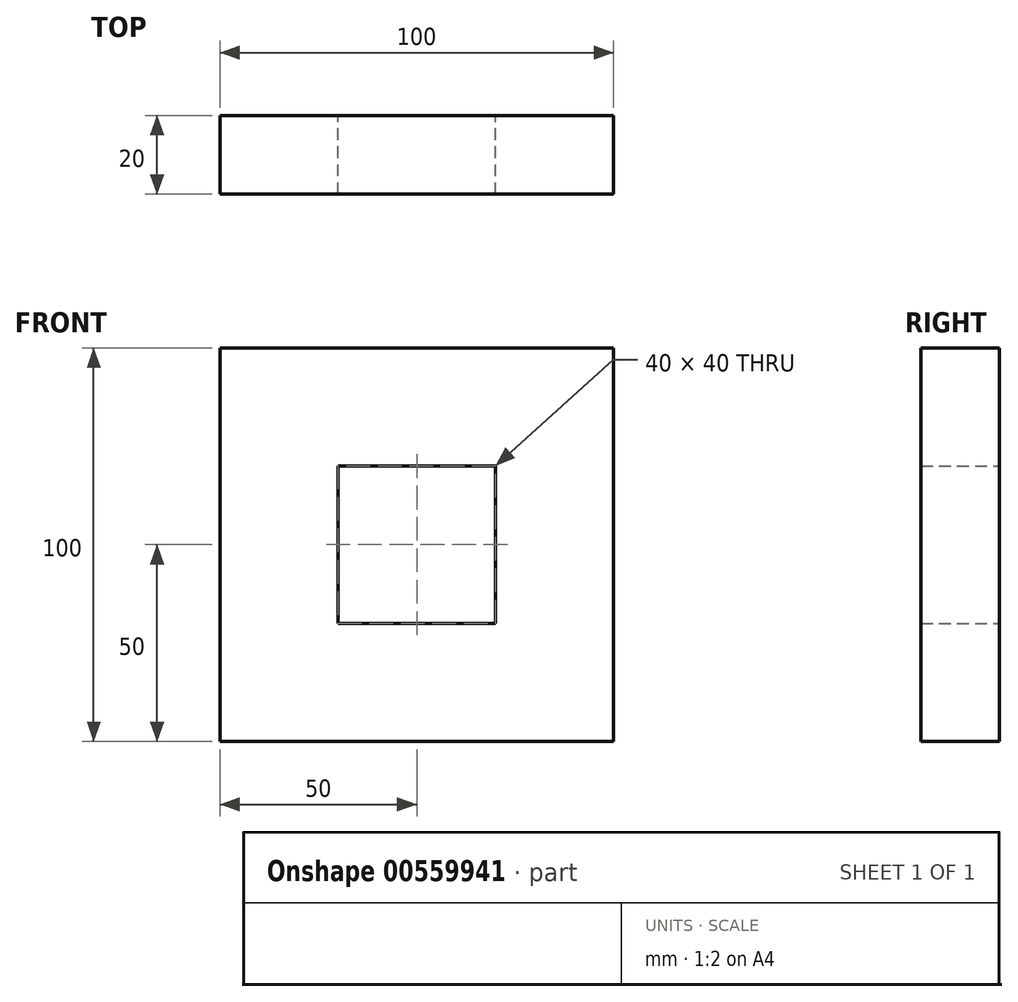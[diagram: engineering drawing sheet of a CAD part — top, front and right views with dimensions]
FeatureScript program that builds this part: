
annotation { "Feature Type Name" : "Feature", "Feature Type Description" : "" }
export const myFeature = defineFeature(function(context is Context, id is Id, definition is map)
    precondition{}
    {
        {
            var Q0;
            Q0=qCreatedBy(makeId("Front.planeOp"),FACE);
            var sketch = newSketch(context, id + "F0", { "sketchPlane" : qUnion([Q0])});
            skLineSegment(sketch, "E0.bottom", {"start": v(50, 50) * mm, "end": v(-50, 50) * mm});
            skLineSegment(sketch, "E0.top", {"start": v(50, -50) * mm, "end": v(-50, -50) * mm});
            skLineSegment(sketch, "E0.left", {"start": v(50, 50) * mm, "end": v(50, -50) * mm});
            skLineSegment(sketch, "E0.right", {"start": v(-50, 50) * mm, "end": v(-50, -50) * mm});
            skPoint(sketch, "E0.middle", {"position": v(0, 0) * mm});
            skLineSegment(sketch, "E1.bottom", {"start": v(20, 20) * mm, "end": v(-20, 20) * mm});
            skLineSegment(sketch, "E1.top", {"start": v(20, -20) * mm, "end": v(-20, -20) * mm});
            skLineSegment(sketch, "E1.left", {"start": v(20, 20) * mm, "end": v(20, -20) * mm});
            skLineSegment(sketch, "E1.right", {"start": v(-20, 20) * mm, "end": v(-20, -20) * mm});
            skSolve(sketch);
        }
        {
            var Q0;
            Q0 = qSketchRegion(id + "F0", true);
            extrude(context, id + "F1", {"entities" : qUnion([Q0]), "depth" : 20 * mm, "offsetDistance" : 25.4 * mm});
        }
    });
